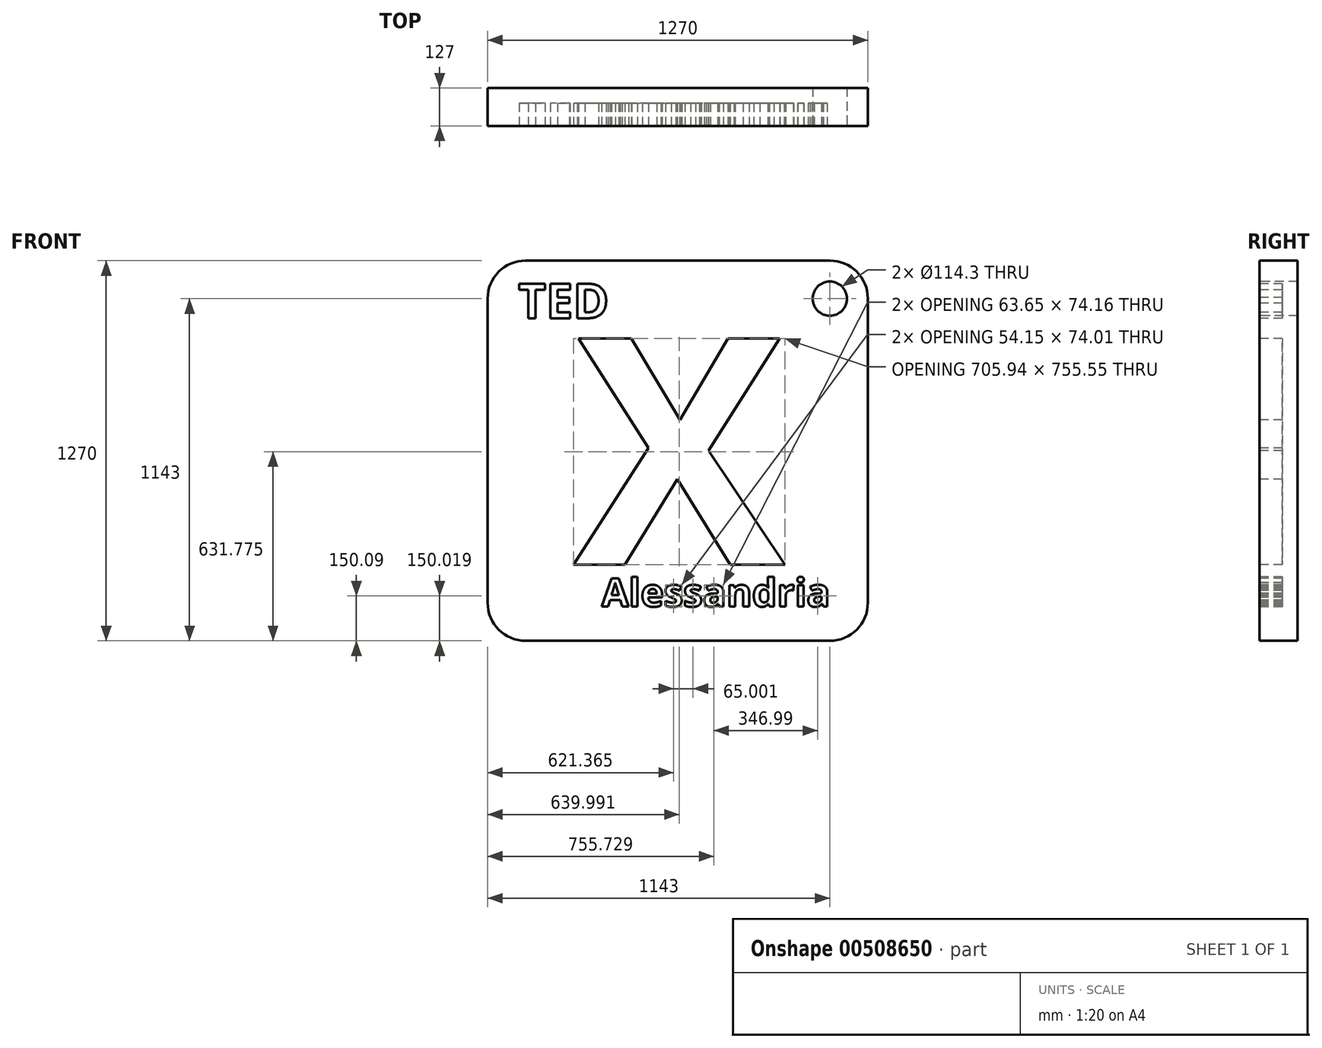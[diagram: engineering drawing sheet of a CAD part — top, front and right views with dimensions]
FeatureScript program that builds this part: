
annotation { "Feature Type Name" : "Feature", "Feature Type Description" : "" }
export const myFeature = defineFeature(function(context is Context, id is Id, definition is map)
    precondition{}
    {
        {
            var Q0;
            Q0=qCreatedBy(makeId("Front.planeOp"),FACE);
            var sketch = newSketch(context, id + "F0", { "sketchPlane" : qUnion([Q0])});
            skLineSegment(sketch, "E0.bottom", {"start": v(635, 635) * mm, "end": v(-635, 635) * mm});
            skLineSegment(sketch, "E0.top", {"start": v(635, -635) * mm, "end": v(-635, -635) * mm});
            skLineSegment(sketch, "E0.left", {"start": v(635, 635) * mm, "end": v(635, -635) * mm});
            skLineSegment(sketch, "E0.right", {"start": v(-635, 635) * mm, "end": v(-635, -635) * mm});
            skPoint(sketch, "E0.middle", {"position": v(0, 0) * mm});
            skSolve(sketch);
        }
        {
            var Q0;
            Q0=makeQuery(id+"F0.imprint","IMPRINT",FACE,{"disambiguationData":[TD([[makeQuery(id+"F0.imprint","IMPRINT",EDGE,{"derivedFrom":sQuery(id+"F0.wireOp",EDGE,"E0.bottom")}),1.0]])]});
            extrude(context, id + "F1", {"entities" : qUnion([Q0]), "depth" : 127 * mm});
        }
        {
            var Q0;
            Q0=makeQuery(id+"F1.opExtrude","CAP_FACE",FACE,{"disambiguationData":[OSD([sQuery(id+"F0.wireOp",EDGE,"E0.bottom"),sQuery(id+"F0.wireOp",EDGE,"E0.top"),sQuery(id+"F0.wireOp",EDGE,"E0.left"),sQuery(id+"F0.wireOp",EDGE,"E0.right")])],"isStart":false});
            var sketch = newSketch(context, id + "F2", { "sketchPlane" : qUnion([Q0])});
            skText(sketch, "E1", { "text": "X", "fontName": "OpenSans-Bold.ttf"});
            const initialGuessF2  = {"E1": [-0.34798, -0.381, 1, 0, 0.762]};
            skSetInitialGuess(sketch, initialGuessF2);
            skSolve(sketch);
        }
        {
            var Q0;
            Q0=makeQuery(id+"F2.imprint","IMPRINT",FACE,{"disambiguationData":[TD([[makeQuery(id+"F2.imprint","IMPRINT",EDGE,{"derivedFrom":sQuery(id+"F2.wireOp",EDGE,"E1.sketch_text.stroke-0")}),-1.0]])]});
            extrude(context, id + "F3", {"entities" : qUnion([Q0]), "operationType" : NewBodyOperationType.REMOVE, "oppositeDirection" : true, "depth" : 76.2 * mm});
        }
        {
            var Q0;
            Q0=makeQuery(id+"F1.opExtrude","CAP_FACE",FACE,{"disambiguationData":[OSD([sQuery(id+"F0.wireOp",EDGE,"E0.bottom"),sQuery(id+"F0.wireOp",EDGE,"E0.top"),sQuery(id+"F0.wireOp",EDGE,"E0.left"),sQuery(id+"F0.wireOp",EDGE,"E0.right")])],"isStart":false});
            var sketch = newSketch(context, id + "F4", { "sketchPlane" : qUnion([Q0])});
            skText(sketch, "E2", { "text": "Alessandria", "fontName": "OpenSans-Bold.ttf"});
            const initialGuessF4  = {"E2": [-0.254, -0.5207, 1, 0, 0.09416]};
            skSetInitialGuess(sketch, initialGuessF4);
            skSolve(sketch);
        }
        {
            var Q0;
            Q0 = qSketchRegion(id + "F4", true);
            extrude(context, id + "F5", {"entities" : qUnion([Q0]), "operationType" : NewBodyOperationType.REMOVE, "oppositeDirection" : true, "depth" : 76.2 * mm});
        }
        {
            var Q0;
            {var subQ0=sQuery(id+"F0.wireOp",EDGE,"E0.left");var subQ1=sQuery(id+"F0.wireOp",EDGE,"E0.top");var subQ2=sQuery(id+"F0.wireOp",EDGE,"E0.right");var subQ3=sQuery(id+"F0.wireOp",EDGE,"E0.bottom");Q0=makeQuery(id+"F5.boolean.opBoolean","SPLIT",FACE,{"disambiguationData":[TD([makeQuery(id+"F1.opExtrude","SWEPT_FACE",FACE,{"disambiguationData":[OSD([subQ3])]})])],"derivedFrom":makeQuery(id+"F1.opExtrude","CAP_FACE",FACE,{"disambiguationData":[OSD([subQ3,subQ1,subQ0,subQ2])],"isStart":false})});}
            var sketch = newSketch(context, id + "F6", { "sketchPlane" : qUnion([Q0])});
            skText(sketch, "E3", { "text": "TED", "fontName": "OpenSans-Bold.ttf"});
            const initialGuessF6  = {"E3": [-0.5334, 0.44245, 1, 0, 0.11635]};
            skSetInitialGuess(sketch, initialGuessF6);
            skSolve(sketch);
        }
        {
            var Q0;
            Q0 = qSketchRegion(id + "F6", true);
            extrude(context, id + "F7", {"entities" : qUnion([Q0]), "operationType" : NewBodyOperationType.REMOVE, "oppositeDirection" : true, "depth" : 76.2 * mm});
        }
        {
            var Q0;
            Q0=makeQuery(id+"F1.opExtrude","SWEPT_EDGE",EDGE,{"disambiguationData":[OSD([sQuery(id+"F0.wireOp",EDGE,"E0.bottom"),sQuery(id+"F0.wireOp",EDGE,"E0.left")])]});
            var Q1;
            Q1=makeQuery(id+"F1.opExtrude","SWEPT_EDGE",EDGE,{"disambiguationData":[OSD([sQuery(id+"F0.wireOp",EDGE,"E0.bottom"),sQuery(id+"F0.wireOp",EDGE,"E0.right")])]});
            var Q2;
            Q2=makeQuery(id+"F1.opExtrude","SWEPT_EDGE",EDGE,{"disambiguationData":[OSD([sQuery(id+"F0.wireOp",EDGE,"E0.top"),sQuery(id+"F0.wireOp",EDGE,"E0.right")])]});
            var Q3;
            Q3=makeQuery(id+"F1.opExtrude","SWEPT_EDGE",EDGE,{"disambiguationData":[OSD([sQuery(id+"F0.wireOp",EDGE,"E0.top"),sQuery(id+"F0.wireOp",EDGE,"E0.left")])]});
            fillet(context, id + "F8", {"entities" : qUnion([Q0, Q1, Q2, Q3]), "radius" : 127 * mm, "tangentPropagation" : true, "allowEdgeOverflow" : false});
        }
        {
            var Q0;
            {var subQ29=sQuery(id+"F0.wireOp",EDGE,"E0.right");var subQ32=sQuery(id+"F0.wireOp",EDGE,"E0.left");var subQ35=sQuery(id+"F0.wireOp",EDGE,"E0.top");var subQ40=sQuery(id+"F0.wireOp",EDGE,"E0.bottom");var subQ41=makeQuery(id+"F1.opExtrude","SWEPT_FACE",FACE,{"disambiguationData":[OSD([subQ40])]});Q0=makeQuery(id+"F7.boolean.opBoolean","SPLIT",FACE,{"disambiguationData":[TD([subQ41])],"derivedFrom":makeQuery(id+"F5.boolean.opBoolean","SPLIT",FACE,{"disambiguationData":[TD([subQ41])],"derivedFrom":makeQuery(id+"F1.opExtrude","CAP_FACE",FACE,{"disambiguationData":[OSD([subQ40,subQ35,subQ32,subQ29])],"isStart":false})})});}
            var sketch = newSketch(context, id + "F9", { "sketchPlane" : qUnion([Q0])});
            skCircle(sketch, "E4", {"center": v(508, 508) * mm, "radius": 57.15 * mm});
            skSolve(sketch);
        }
        {
            var Q0;
            Q0=makeQuery(id+"F9.imprint","IMPRINT",FACE,{"disambiguationData":[TD([[makeQuery(id+"F9.imprint","IMPRINT",EDGE,{"derivedFrom":sQuery(id+"F9.wireOp",EDGE,"E4")}),1.0]])]});
            extrude(context, id + "F10", {"entities" : qUnion([Q0]), "operationType" : NewBodyOperationType.REMOVE, "endBound" : BoundingType.UP_TO_NEXT, "oppositeDirection" : true, "depth" : 25.4 * mm});
        }
    });
